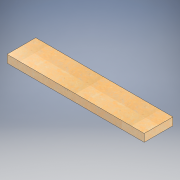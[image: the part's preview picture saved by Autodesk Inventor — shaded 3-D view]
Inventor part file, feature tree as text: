
AUTODESK INVENTOR PART (.ipt)
format: ipt  version: 2022.2 (Build 262287010, 287A)  size: 126,464 bytes
history: native  units: in
note: dims shown in document units (in); Inventor stores cm internally (conversion verified against a paired STEP export)
features: extrude x1, sketch x1
ambient origin geometry x8: Origin, YZ Plane, XZ Plane, XY Plane, X Axis, Y Axis, Z Axis, Center Point
bodies: Solid1 (feature_tree)
feature tree (2):
  extrude  "Extrusion1"  Depth=15.0in
  sketch  "Sketch1"  dims[d0=71.625in d1=15.0in d2=4.0in d3=0.0in]
